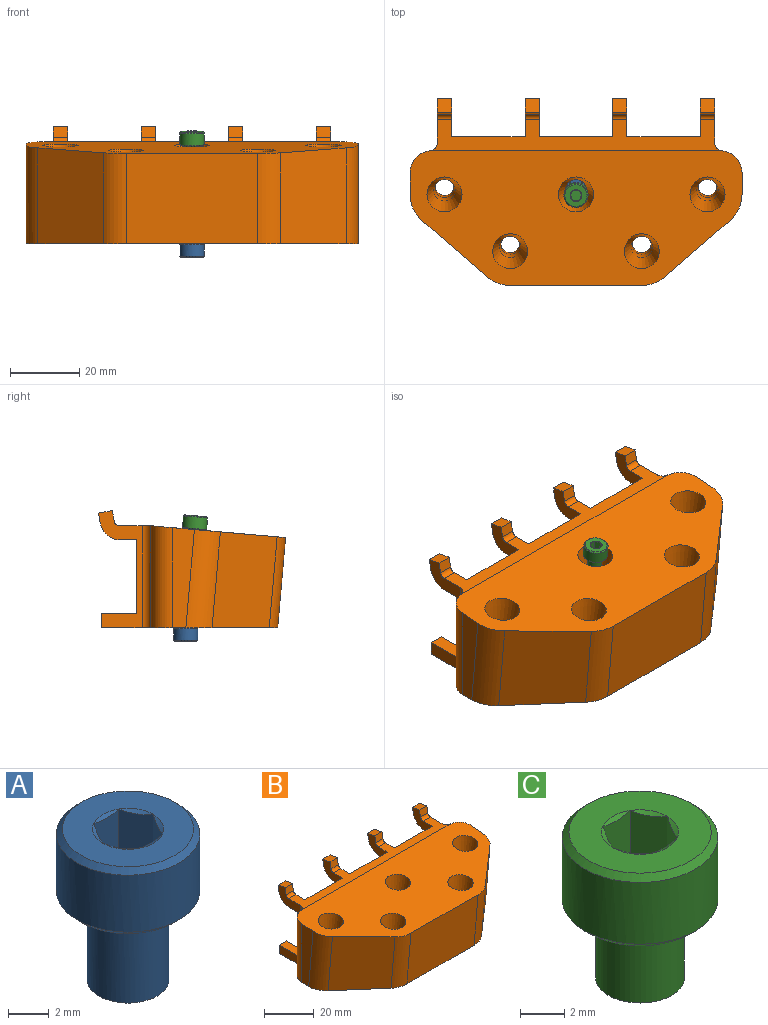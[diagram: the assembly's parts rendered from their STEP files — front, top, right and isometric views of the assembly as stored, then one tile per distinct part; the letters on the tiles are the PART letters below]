
ASSEMBLY  parts=3 mates=2
PART A: 20 faces, bbox 7x7x9 mm
  f0: plane 6.4x6.4mm, normal (0,0,1), area 22.7mm2, adj f5,f6,f7,f8,f9,f10,f19
  f1: plane 4x4mm, normal (0,0,-1), area 12.6mm2, adj f2
  f2: cylinder r=2mm len=5mm, axis (0,0,1), area 62.8mm2, adj f1,f3
  f3: plane 6.4x6.4mm, normal (0,0,-1), area 19.6mm2, adj f2,f18
  f4: cylinder r=3.5mm len=7mm, axis (0,0,1), area 74.8mm2, adj f18,f19
  f5: sphere r=3.25mm, area 0.3mm2, adj f0,f12
  f6: sphere r=3.25mm, area 0.3mm2, adj f0,f13
  f7: sphere r=3.25mm, area 0.3mm2, adj f0,f14
  f8: sphere r=3.25mm, area 0.3mm2, adj f0,f15
  f9: sphere r=3.25mm, area 0.3mm2, adj f0,f16
  f10: sphere r=3.25mm, area 0.3mm2, adj f0,f17
  f11: plane 3.46x3mm, normal (0,0,1), area 7.8mm2, adj f12,f13,f14,f15,f16,f17
  f12: plane 2.5x1.5mm, normal (-0.87,0.5,0), area 4.2mm2, adj f5,f11,f13,f17
  f13: plane 2.5x1.73mm, normal (0,1,0), area 4.2mm2, adj f6,f11,f12,f14
  f14: plane 2.5x1.5mm, normal (0.87,0.5,0), area 4.2mm2, adj f7,f11,f13,f15
  f15: plane 2.5x1.5mm, normal (0.87,-0.5,0), area 4.2mm2, adj f8,f11,f14,f16
  f16: plane 2.5x1.73mm, normal (0,-1,0), area 4.2mm2, adj f9,f11,f15,f17
  f17: plane 2.5x1.5mm, normal (-0.87,-0.5,0), area 4.2mm2, adj f10,f11,f12,f16
  f18: cone r=3.5mm half-angle=45deg, axis (0,0,1), area 8.9mm2, adj f3,f4
  f19: cone r=3.2mm half-angle=45deg, axis (0,0,-1), area 8.9mm2, adj f0,f4
PART B: 108 faces, bbox 119x66.8x75.3 mm
  f0: plane 25.76x3.82mm, normal (1,0,0), area 91.5mm2, adj f2,f3,f10,f97,f101
  f1: plane 25.76x3.82mm, normal (-1,0,0), area 91.5mm2, adj f2,f10,f88,f98,f105
  f2: plane 89.97x33.85mm, normal (0,0.09,-1), area 1661.9mm2, adj f0,f1,f3,f79,f80,f81,f87,f88
  f3: cone r=8.23mm half-angle=7.5deg, axis (0,-0.09,1), area 378.8mm2, adj f0,f2,f4,f101,f102
  f4: torus R=53.55mm, axis (0,0.09,-1), area 230.5mm2, adj f3,f86,f101,f102
  f5: plane 11.9x11.85mm, normal (0,0,-1), area 86.9mm2, adj f65,f86
  f6: plane 11.9x11.85mm, normal (0,0,-1), area 86.9mm2, adj f64,f85
  f7: plane 11.9x11.85mm, normal (0,0,-1), area 86.9mm2, adj f63,f84
  f8: plane 11.9x11.85mm, normal (0,0,-1), area 86.9mm2, adj f62,f83
  f9: plane 11.9x11.85mm, normal (0,0,-1), area 86.9mm2, adj f61,f82
  f10: plane 96.3x51.23mm, normal (0,0,-1), area 816.1mm2, adj f0,f1,f11,f12,f14,f16,f17,f42
  f11: plane 28.95x6.3mm, normal (-1,0,0), area 145.4mm2, adj f10,f57,f59,f76
  f12: plane 10.35x4.1mm, normal (1,0,0), area 42.4mm2, adj f10,f15,f16,f17
  f13: plane 11.16x8.5mm, normal (1,0,0), area 53.7mm2, adj f17,f18,f19,f20,f21,f22,f23,f24
  f14: plane 33.9x12.67mm, normal (-1,0,0), area 140.7mm2, adj f10,f15,f16,f17,f18,f19,f20,f21
  f15: plane 10.35x4.1mm, normal (0,0,1), area 42.4mm2, adj f12,f14,f16,f17
  f16: plane 4.1x4.1mm, normal (0,1,0), area 16.8mm2, adj f10,f12,f14,f15
  f17: plane 80.3x29.5mm, normal (0,1,0), area 2268.1mm2, adj f10,f12,f13,f14,f15,f18,f19,f25
  f18: plane 84.38x9.09mm, normal (0,0,1), area 407.3mm2, adj f13,f14,f17,f23,f25,f26,f31,f33
  f19: plane 4.76x4.1mm, normal (0,0,-1), area 19.5mm2, adj f13,f14,f17,f24
  f20: plane 4.1x2.83mm, normal (0,0.98,-0.17), area 11.8mm2, adj f13,f14,f21,f24
  f21: plane 4.1x4.04mm, normal (0,0.17,0.98), area 16.8mm2, adj f13,f14,f20,f22
  f22: plane 4.1x3.16mm, normal (0,-0.98,0.17), area 13.2mm2, adj f13,f14,f21,f23
  f23: cylinder r=1.5mm len=4.1mm, axis (1,0,0), area 8.6mm2, adj f13,f14,f18,f22
  f24: cylinder r=6mm len=5.91mm, axis (1,0,0), area 34.4mm2, adj f13,f14,f19,f20
  f25: plane 11.16x8.5mm, normal (-1,0,0), area 53.7mm2, adj f17,f18,f27,f28,f29,f30,f31,f32
  f26: plane 11.16x8.5mm, normal (1,0,0), area 53.7mm2, adj f17,f18,f27,f28,f29,f30,f31,f32
  f27: plane 4.76x4.1mm, normal (0,0,-1), area 19.5mm2, adj f17,f25,f26,f32
  f28: plane 4.1x2.83mm, normal (0,0.98,-0.17), area 11.8mm2, adj f25,f26,f29,f32
  f29: plane 4.1x4.04mm, normal (0,0.17,0.98), area 16.8mm2, adj f25,f26,f28,f30
  f30: plane 4.1x3.16mm, normal (0,-0.98,0.17), area 13.2mm2, adj f25,f26,f29,f31
  f31: cylinder r=1.5mm len=4.1mm, axis (1,0,0), area 8.6mm2, adj f18,f25,f26,f30
  f32: cylinder r=6mm len=5.91mm, axis (1,0,0), area 34.4mm2, adj f25,f26,f27,f28
  f33: plane 11.16x8.5mm, normal (-1,0,0), area 53.7mm2, adj f17,f18,f35,f36,f37,f38,f39,f40
  f34: plane 11.16x8.5mm, normal (1,0,0), area 53.7mm2, adj f17,f18,f35,f36,f37,f38,f39,f40
  f35: plane 4.76x4.1mm, normal (0,0,-1), area 19.5mm2, adj f17,f33,f34,f40
  f36: plane 4.1x2.83mm, normal (0,0.98,-0.17), area 11.8mm2, adj f33,f34,f37,f40
  f37: plane 4.1x4.04mm, normal (0,0.17,0.98), area 16.8mm2, adj f33,f34,f36,f38
  f38: plane 4.1x3.16mm, normal (0,-0.98,0.17), area 13.2mm2, adj f33,f34,f37,f39
  f39: cylinder r=1.5mm len=4.1mm, axis (1,0,0), area 8.6mm2, adj f18,f33,f34,f38
  f40: cylinder r=6mm len=5.91mm, axis (1,0,0), area 34.4mm2, adj f33,f34,f35,f36
  f41: plane 11.16x8.5mm, normal (-1,0,0), area 53.7mm2, adj f17,f18,f46,f47,f48,f49,f50,f51
  f42: plane 10.35x4.1mm, normal (-1,0,0), area 42.4mm2, adj f10,f17,f44,f45
  f43: plane 33.9x12.67mm, normal (1,0,0), area 140.7mm2, adj f10,f17,f18,f44,f45,f46,f47,f48
  f44: plane 10.35x4.1mm, normal (0,0,1), area 42.4mm2, adj f17,f42,f43,f45
  f45: plane 4.1x4.1mm, normal (0,1,0), area 16.8mm2, adj f10,f42,f43,f44
  f46: plane 4.76x4.1mm, normal (0,0,-1), area 19.5mm2, adj f17,f41,f43,f51
  f47: plane 4.1x2.83mm, normal (0,0.98,-0.17), area 11.8mm2, adj f41,f43,f48,f51
  f48: plane 4.1x4.04mm, normal (0,0.17,0.98), area 16.8mm2, adj f41,f43,f47,f49
  f49: plane 4.1x3.16mm, normal (0,-0.98,0.17), area 13.2mm2, adj f41,f43,f48,f50
  f50: cylinder r=1.5mm len=4.1mm, axis (1,0,0), area 8.6mm2, adj f18,f41,f43,f49
  f51: cylinder r=6mm len=5.91mm, axis (1,0,0), area 34.4mm2, adj f41,f43,f46,f47
  f52: plane 28.95x6.3mm, normal (1,0,0), area 145.4mm2, adj f10,f53,f57,f77
  f53: cylinder r=10mm len=29.05mm, axis (0,-0.09,1), area 241.4mm2, adj f10,f52,f54,f57
  f54: plane 27.74x19.05mm, normal (0.65,-0.75,-0.07), area 683.6mm2, adj f10,f53,f55,f57
  f55: cylinder r=10mm len=26.51mm, axis (0,-0.09,1), area 187.7mm2, adj f10,f54,f56,f57
  f56: plane 38.1x26.08mm, normal (0,-1,-0.09), area 997.6mm2, adj f10,f55,f57,f58
  f57: plane 96.2x39.06mm, normal (0,-0.09,1), area 2784.8mm2, adj f11,f18,f52,f53,f54,f55,f56,f58
  f58: cylinder r=10mm len=26.51mm, axis (0,-0.09,1), area 187.7mm2, adj f10,f56,f57,f60
  f59: cylinder r=10mm len=29.05mm, axis (0,-0.09,1), area 241.4mm2, adj f10,f11,f57,f60
  f60: plane 27.74x19.05mm, normal (-0.65,-0.75,-0.07), area 683.6mm2, adj f10,f57,f58,f59
  f61: cylinder r=2.75mm len=6.73mm, axis (0,-0.09,1), area 104.2mm2, adj f9,f71
  f62: cylinder r=2.75mm len=6.73mm, axis (0,-0.09,1), area 104.2mm2, adj f8,f72
  f63: cylinder r=2.75mm len=8.17mm, axis (0,-0.09,1), area 129.2mm2, adj f7,f73
  f64: cylinder r=2.75mm len=8.17mm, axis (0,-0.09,1), area 129.2mm2, adj f6,f74
  f65: cylinder r=2.75mm len=8.17mm, axis (0,-0.09,1), area 129.2mm2, adj f5,f75
  f66: cone r=5.08mm half-angle=7.5deg, axis (0,-0.09,1), area 377mm2, adj f57,f75
  f67: cone r=5.08mm half-angle=7.5deg, axis (0,-0.09,1), area 377mm2, adj f57,f74
  f68: cone r=5.08mm half-angle=7.5deg, axis (0,-0.09,1), area 377mm2, adj f57,f73
  f69: cone r=5.08mm half-angle=7.5deg, axis (0,-0.09,1), area 377mm2, adj f57,f72
  f70: cone r=5.08mm half-angle=7.5deg, axis (0,-0.09,1), area 377mm2, adj f57,f71
  f71: torus R=53.55mm, axis (0,0.09,-1), area 121mm2, adj f61,f70
  f72: torus R=53.55mm, axis (0,0.09,-1), area 121mm2, adj f62,f69
  f73: torus R=53.55mm, axis (0,0.09,-1), area 121mm2, adj f63,f68
  f74: torus R=53.55mm, axis (0,0.09,-1), area 121mm2, adj f64,f67
  f75: torus R=53.55mm, axis (0,0.09,-1), area 121mm2, adj f65,f66
  f76: cylinder r=6.35mm len=29.5mm, axis (0,0,-1), area 272.4mm2, adj f10,f11,f57,f107
  f77: cylinder r=6.35mm len=29.5mm, axis (0,0,1), area 272.4mm2, adj f10,f52,f57,f106
  f78: plane 73.95x26.33mm, normal (0,-1,0), area 1946.9mm2, adj f10,f79,f80,f81
  f79: plane 26.33x4mm, normal (1,0,0), area 104.8mm2, adj f2,f10,f78,f80,f96
  f80: plane 73.95x0.69mm, normal (0,0,-1), area 50.8mm2, adj f2,f78,f79,f81
  f81: plane 26.33x4mm, normal (-1,0,0), area 104.8mm2, adj f2,f10,f78,f80,f95
  f82: cylinder r=5.92mm len=12.38mm, axis (0,-0.09,1), area 224.5mm2, adj f9,f91
  f83: cylinder r=5.92mm len=12.38mm, axis (0,-0.09,1), area 224.5mm2, adj f8,f92
  f84: cylinder r=5.92mm len=12.5mm, axis (0,-0.09,1), area 278.3mm2, adj f7,f93
  f85: cylinder r=5.92mm len=12.5mm, axis (0,-0.09,1), area 278.3mm2, adj f6,f94
  f86: cylinder r=5.92mm len=12.5mm, axis (0,-0.09,1), area 278.3mm2, adj f4,f5
  f87: cone r=8.23mm half-angle=7.5deg, axis (0,-0.09,1), area 523.5mm2, adj f2,f94
  f88: cone r=8.23mm half-angle=7.5deg, axis (0,-0.09,1), area 378.8mm2, adj f1,f2,f93,f104,f105
  f89: cone r=8.23mm half-angle=7.5deg, axis (0,-0.09,1), area 351.2mm2, adj f2,f92,f103,f104
  f90: cone r=8.23mm half-angle=7.5deg, axis (0,-0.09,1), area 351.2mm2, adj f2,f91,f102,f103
  f91: torus R=53.55mm, axis (0,0.09,-1), area 219.9mm2, adj f82,f90,f99,f102,f103
  f92: torus R=53.55mm, axis (0,0.09,-1), area 219.9mm2, adj f83,f89,f100,f103,f104
  f93: torus R=53.55mm, axis (0,0.09,-1), area 230.5mm2, adj f84,f88,f104,f105
  f94: torus R=53.55mm, axis (0,0.09,-1), area 237.4mm2, adj f85,f87
  f95: plane 26.04x4.77mm, normal (0,-1,0), area 124.3mm2, adj f2,f10,f81,f98
  f96: plane 26.04x4.77mm, normal (0,-1,0), area 124.3mm2, adj f2,f10,f79,f97
  f97: cylinder r=3.17mm len=26.04mm, axis (0,0,-1), area 129.2mm2, adj f0,f2,f10,f96
  f98: cylinder r=3.17mm len=26.04mm, axis (0,0,1), area 129.2mm2, adj f1,f2,f10,f95
  f99: extruded ~10.42x4.47mm, area 45.9mm2, adj f10,f91,f102,f103
  f100: extruded ~10.42x4.47mm, area 45.9mm2, adj f10,f92,f103,f104
  f101: extruded ~19.01x5.18mm, area 84.9mm2, adj f0,f3,f4,f10,f102
  f102: plane 24.55x19.05mm, normal (0.66,0.75,0), area 507.3mm2, adj f2,f3,f4,f10,f90,f91,f99,f101
  f103: plane 38.1x23.38mm, normal (0,1,0), area 773.5mm2, adj f2,f10,f89,f90,f91,f92,f99,f100
  f104: plane 24.55x19.05mm, normal (-0.66,0.75,0), area 507.3mm2, adj f2,f10,f88,f89,f92,f93,f100,f105
  f105: extruded ~19.01x5.18mm, area 84.9mm2, adj f1,f10,f88,f93,f104
  f106: cylinder r=2.54mm len=29.5mm, axis (0,0,1), area 109.8mm2, adj f10,f18,f43,f57,f77
  f107: cylinder r=2.54mm len=29.5mm, axis (0,0,-1), area 109.8mm2, adj f10,f14,f18,f57,f76
PART C: 20 faces, bbox 7x7x8 mm
  f0: plane 6.4x6.4mm, normal (0,0,1), area 22.7mm2, adj f5,f6,f7,f8,f9,f10,f19
  f1: plane 4x4mm, normal (0,0,-1), area 12.6mm2, adj f2
  f2: cylinder r=2mm len=4mm, axis (0,0,1), area 50.3mm2, adj f1,f3
  f3: plane 6.4x6.4mm, normal (0,0,-1), area 19.6mm2, adj f2,f18
  f4: cylinder r=3.5mm len=7mm, axis (0,0,1), area 74.8mm2, adj f18,f19
  f5: sphere r=3.25mm, area 0.3mm2, adj f0,f12
  f6: sphere r=3.25mm, area 0.3mm2, adj f0,f13
  f7: sphere r=3.25mm, area 0.3mm2, adj f0,f14
  f8: sphere r=3.25mm, area 0.3mm2, adj f0,f15
  f9: sphere r=3.25mm, area 0.3mm2, adj f0,f16
  f10: sphere r=3.25mm, area 0.3mm2, adj f0,f17
  f11: plane 3.46x3mm, normal (0,0,1), area 7.8mm2, adj f12,f13,f14,f15,f16,f17
  f12: plane 2.5x1.5mm, normal (-0.87,0.5,0), area 4.2mm2, adj f5,f11,f13,f17
  f13: plane 2.5x1.73mm, normal (0,1,0), area 4.2mm2, adj f6,f11,f12,f14
  f14: plane 2.5x1.5mm, normal (0.87,0.5,0), area 4.2mm2, adj f7,f11,f13,f15
  f15: plane 2.5x1.5mm, normal (0.87,-0.5,0), area 4.2mm2, adj f8,f11,f14,f16
  f16: plane 2.5x1.73mm, normal (0,-1,0), area 4.2mm2, adj f9,f11,f15,f17
  f17: plane 2.5x1.5mm, normal (-0.87,-0.5,0), area 4.2mm2, adj f10,f11,f12,f16
  f18: cone r=3.5mm half-angle=45deg, axis (0,0,1), area 8.9mm2, adj f3,f4
  f19: cone r=3.2mm half-angle=45deg, axis (0,0,-1), area 8.9mm2, adj f0,f4
PLACE A rot(axis=(1,0,0),180deg) t=(39.67,2.19,10.85)mm
PLACE B t=(1.57,16.36,12.9)mm fixed
PLACE C rot(axis=(1,0,0),5deg) t=(39.67,-0.3,39.24)mm
MATE fastened A.f18 <-> B.f6  axis (0,0,1) through (39.67,2.19,10.85)mm
MATE fastened C.f2 <-> B.f64  axis (0,0.09,-1) through (39.67,-0.3,39.24)mm
